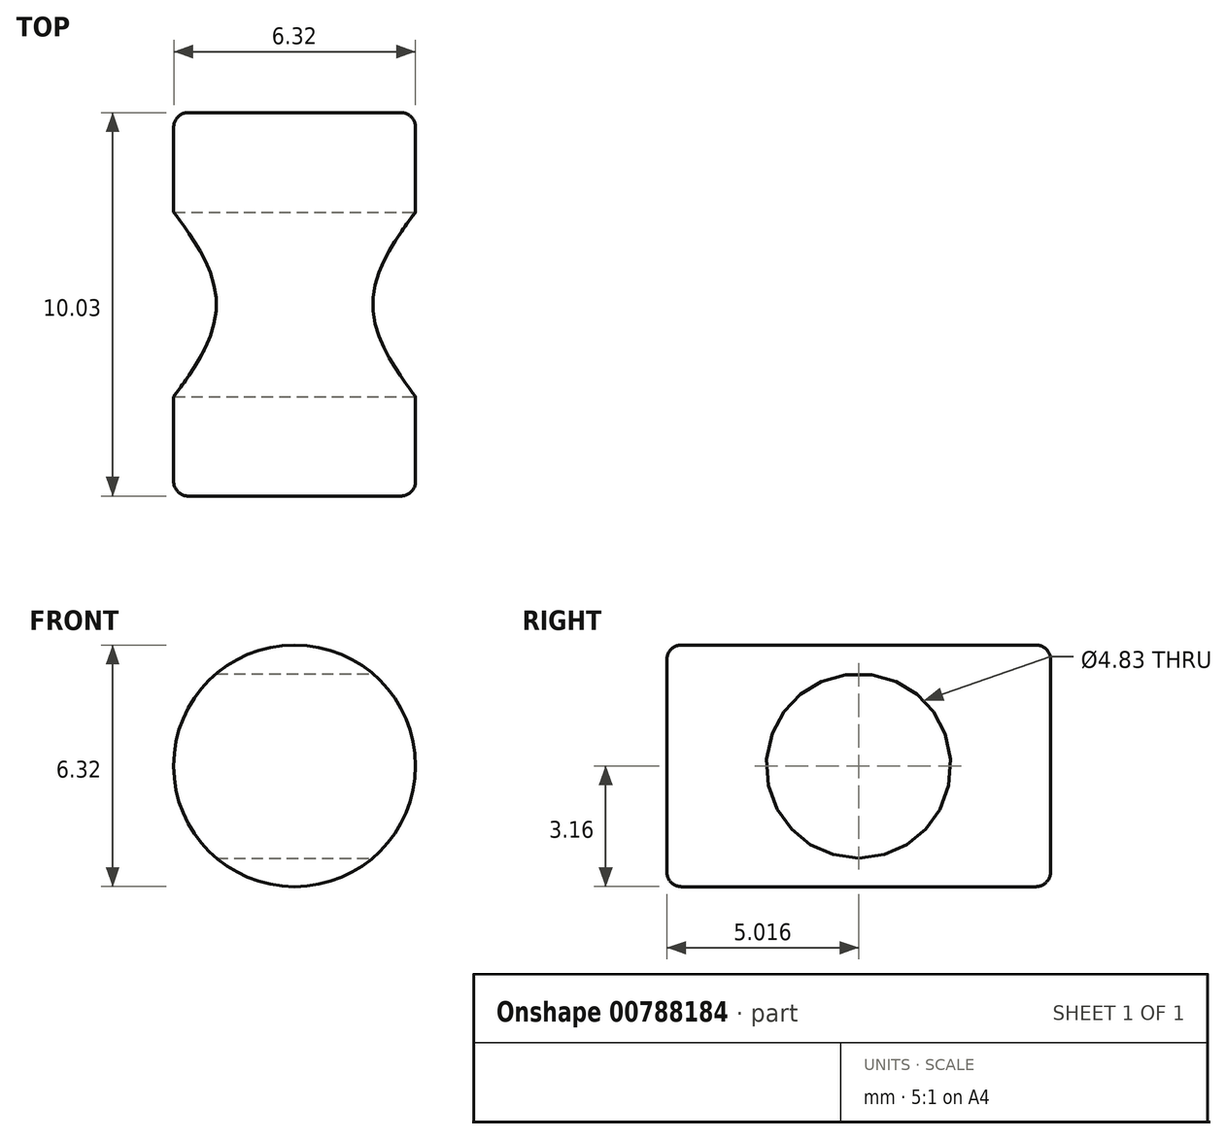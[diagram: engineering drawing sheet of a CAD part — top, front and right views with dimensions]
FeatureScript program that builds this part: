
annotation { "Feature Type Name" : "Feature", "Feature Type Description" : "" }
export const myFeature = defineFeature(function(context is Context, id is Id, definition is map)
    precondition{}
    {
        {
            var Q0;
            Q0=qCreatedBy(makeId("Front.planeOp"),FACE);
            var sketch = newSketch(context, id + "F0", { "sketchPlane" : qUnion([Q0])});
            skCircle(sketch, "E0", {"center": v(0, 0) * mm, "radius": 3.16 * mm});
            skSolve(sketch);
        }
        {
            var Q0;
            Q0=makeQuery(id+"F0.imprint","IMPRINT",FACE,{"disambiguationData":[TD([[makeQuery(id+"F0.imprint","IMPRINT",EDGE,{"derivedFrom":sQuery(id+"F0.wireOp",EDGE,"E0")}),1.0]])]});
            extrude(context, id + "F1", {"entities" : qUnion([Q0]), "oppositeDirection" : true, "depth" : 10.03 * mm});
        }
        {
            var Q0;
            Q0=qCreatedBy(makeId("Right.planeOp"),FACE);
            var sketch = newSketch(context, id + "F2", { "sketchPlane" : qUnion([Q0])});
            skCircle(sketch, "E1", {"center": v(5.02, 0) * mm, "radius": 2.41 * mm});
            skSolve(sketch);
        }
        {
            var Q0;
            Q0=qSketchRegion(id+"F2",true);
            extrude(context, id + "F3", {"entities" : qUnion([Q0]), "operationType" : NewBodyOperationType.REMOVE, "endBound" : BoundingType.SYMMETRIC, "oppositeDirection" : true, "depth" : 7.62 * mm});
        }
        {
            var Q0;
            Q0=makeQuery(id+"F1.opExtrude","CAP_EDGE",EDGE,{"disambiguationData":[OSD([sQuery(id+"F0.wireOp",EDGE,"E0")])],"isStart":false});
            var Q1;
            Q1=makeQuery(id+"F1.opExtrude","CAP_EDGE",EDGE,{"disambiguationData":[OSD([sQuery(id+"F0.wireOp",EDGE,"E0")])],"isStart":true});
            fillet(context, id + "F4", {"entities" : qUnion([Q0, Q1]), "radius" : 0.38 * mm, "tangentPropagation" : true, "allowEdgeOverflow" : false});
        }
    });
